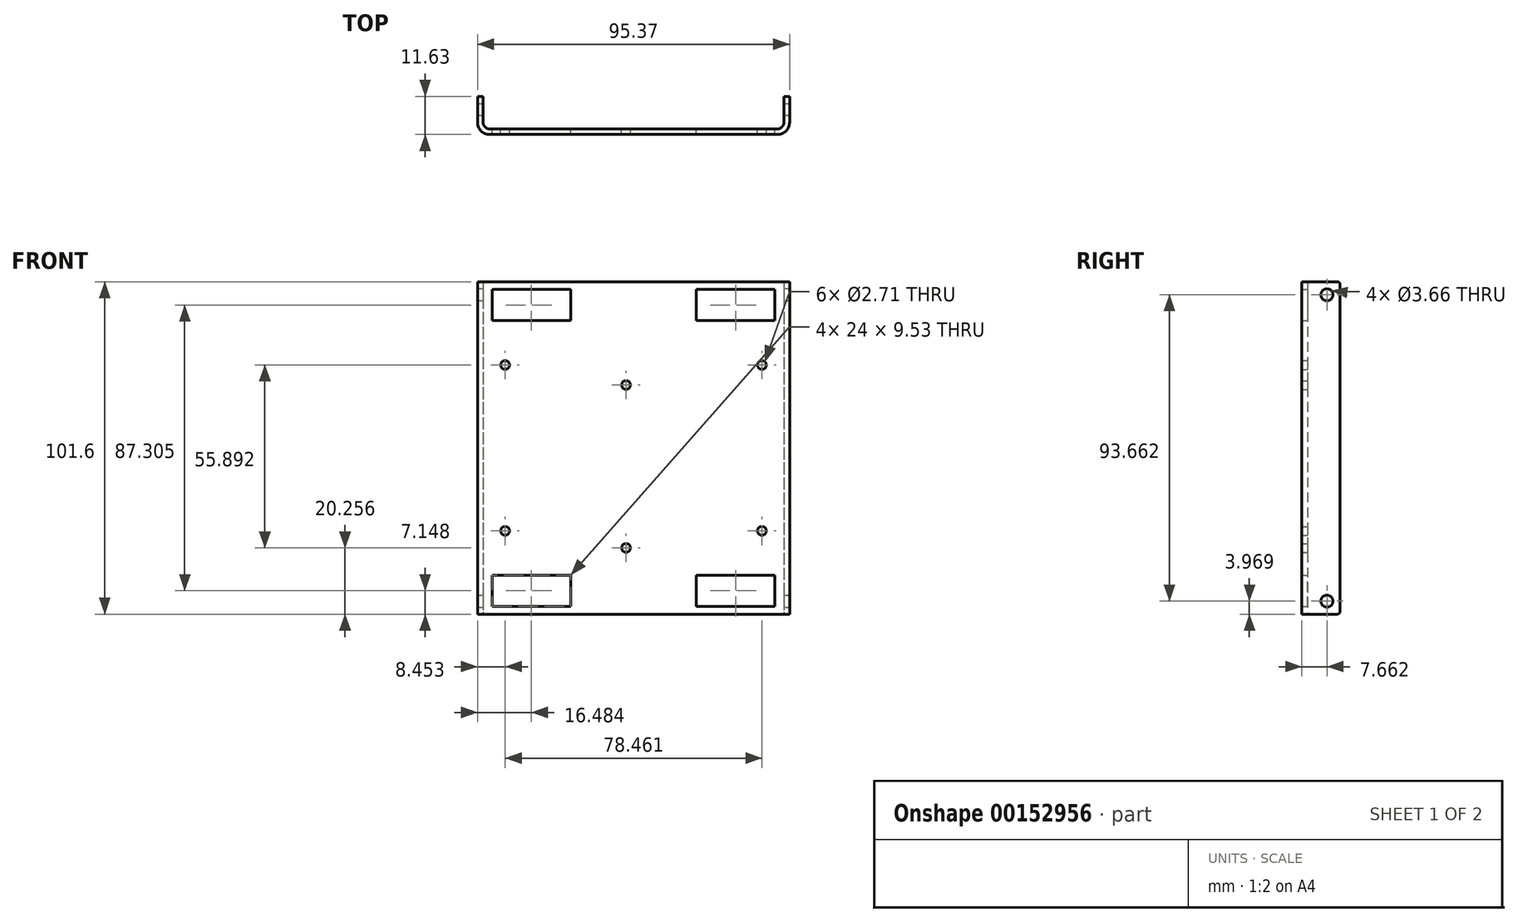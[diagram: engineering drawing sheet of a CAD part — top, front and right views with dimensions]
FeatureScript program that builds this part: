
annotation { "Feature Type Name" : "Feature", "Feature Type Description" : "" }
export const myFeature = defineFeature(function(context is Context, id is Id, definition is map)
    precondition{}
    {
        {
            var Q0;
            Q0=qCreatedBy(makeId("Top.planeOp"),FACE);
            var sketch = newSketch(context, id + "F0", { "sketchPlane" : qUnion([Q0])});
            skLineSegment(sketch, "E0.bottom", {"start": v(0, 0) * mm, "end": v(-91.95, 0) * mm});
            skLineSegment(sketch, "E0.top", {"start": v(1.7, -1.7) * mm, "end": v(-93.66, -1.7) * mm});
            skLineSegment(sketch, "E1.top", {"start": v(-91.95, 9.92) * mm, "end": v(-93.66, 9.92) * mm});
            skLineSegment(sketch, "E1.left", {"start": v(-91.95, 0) * mm, "end": v(-91.95, 9.92) * mm});
            skLineSegment(sketch, "E1.right", {"start": v(-93.66, -1.7) * mm, "end": v(-93.66, 9.92) * mm});
            skLineSegment(sketch, "E2.top", {"start": v(0, 9.92) * mm, "end": v(1.7, 9.92) * mm});
            skLineSegment(sketch, "E2.left", {"start": v(0, 0) * mm, "end": v(0, 9.92) * mm});
            skLineSegment(sketch, "E2.right", {"start": v(1.7, -1.7) * mm, "end": v(1.7, 9.92) * mm});
            skLineSegment(sketch, "E3", {"start": v(-45.98, 0) * mm, "end": v(-45.98, -1.7) * mm, "construction": true});
            skSolve(sketch);
        }
        {
            var Q0;
            Q0=qSketchRegion(id+"F0",true);
            extrude(context, id + "F1", {"entities" : qUnion([Q0]), "depth" : 101.6 * mm});
        }
        {
            var Q0;
            Q0=makeQuery(id+"F1.opExtrude","SWEPT_EDGE",EDGE,{"disambiguationData":[OSD([sQuery(id+"F0.wireOp",EDGE,"E0.top"),sQuery(id+"F0.wireOp",EDGE,"E2.right")])]});
            var Q1;
            Q1=makeQuery(id+"F1.opExtrude","SWEPT_EDGE",EDGE,{"disambiguationData":[OSD([sQuery(id+"F0.wireOp",EDGE,"E0.top"),sQuery(id+"F0.wireOp",EDGE,"E1.right")])]});
            var Q2;
            Q2=makeQuery(id+"FqNnmMD7oaRdpTN_1.opExtrude","CAP_EDGE",EDGE,{"disambiguationData":[OSD([sQuery(id+"FY5sMr6MULj5lJw_1.wireOp",EDGE,"W42EfhJi-fDm4-L9BW-folL-irsYfDskuzBk.top")])],"isStart":false});
            fillet(context, id + "F2", {"entities" : qUnion([Q0, Q1, Q2]), "radius" : 3.7 * mm, "tangentPropagation" : true, "allowEdgeOverflow" : false});
        }
        {
            var Q0;
            Q0=makeQuery(id+"F1.opExtrude","SWEPT_EDGE",EDGE,{"disambiguationData":[OSD([sQuery(id+"F0.wireOp",EDGE,"E0.bottom"),sQuery(id+"F0.wireOp",EDGE,"E2.left")])]});
            var Q1;
            Q1=makeQuery(id+"F1.opExtrude","SWEPT_EDGE",EDGE,{"disambiguationData":[OSD([sQuery(id+"F0.wireOp",EDGE,"E0.bottom"),sQuery(id+"F0.wireOp",EDGE,"E1.left")])]});
            fillet(context, id + "F3", {"entities" : qUnion([Q0, Q1]), "radius" : 1.98 * mm, "tangentPropagation" : true, "allowEdgeOverflow" : false});
        }
        {
            var Q0;
            Q0=makeQuery(id+"F1.opExtrude","SWEPT_FACE",FACE,{"disambiguationData":[OSD([sQuery(id+"F0.wireOp",EDGE,"E0.bottom")])]});
            var sketch = newSketch(context, id + "F4", { "sketchPlane" : qUnion([Q0])});
            skLineSegment(sketch, "E4", {"start": v(45.98, 101.6) * mm, "end": v(45.98, 0) * mm, "construction": true});
            skLineSegment(sketch, "E5.bottom", {"start": v(77.18, 94.45) * mm, "end": v(14.78, 94.45) * mm, "construction": true});
            skLineSegment(sketch, "E5.top", {"start": v(77.18, 7.15) * mm, "end": v(14.78, 7.15) * mm, "construction": true});
            skLineSegment(sketch, "E5.left", {"start": v(77.18, 94.45) * mm, "end": v(77.18, 7.15) * mm, "construction": true});
            skLineSegment(sketch, "E5.right", {"start": v(14.78, 94.45) * mm, "end": v(14.78, 7.15) * mm, "construction": true});
            skPoint(sketch, "E5.middle", {"position": v(45.98, 50.8) * mm});
            skLineSegment(sketch, "E6.bottom", {"start": v(89.18, 99.22) * mm, "end": v(65.18, 99.22) * mm});
            skLineSegment(sketch, "E6.top", {"start": v(89.18, 89.69) * mm, "end": v(65.18, 89.69) * mm});
            skLineSegment(sketch, "E6.left", {"start": v(89.18, 99.22) * mm, "end": v(89.18, 89.69) * mm});
            skLineSegment(sketch, "E6.right", {"start": v(65.18, 99.22) * mm, "end": v(65.18, 89.69) * mm});
            skPoint(sketch, "E6.middle", {"position": v(77.18, 94.45) * mm});
            skLineSegment(sketch, "E7.bottom", {"start": v(89.18, 2.38) * mm, "end": v(65.18, 2.38) * mm});
            skLineSegment(sketch, "E7.top", {"start": v(89.18, 11.91) * mm, "end": v(65.18, 11.91) * mm});
            skLineSegment(sketch, "E7.left", {"start": v(89.18, 2.38) * mm, "end": v(89.18, 11.91) * mm});
            skLineSegment(sketch, "E7.right", {"start": v(65.18, 2.38) * mm, "end": v(65.18, 11.91) * mm});
            skPoint(sketch, "E7.middle", {"position": v(77.18, 7.15) * mm});
            skLineSegment(sketch, "E8.bottom", {"start": v(2.78, 2.38) * mm, "end": v(26.78, 2.38) * mm});
            skLineSegment(sketch, "E8.top", {"start": v(2.78, 11.91) * mm, "end": v(26.78, 11.91) * mm});
            skLineSegment(sketch, "E8.left", {"start": v(2.78, 2.38) * mm, "end": v(2.78, 11.91) * mm});
            skLineSegment(sketch, "E8.right", {"start": v(26.78, 2.38) * mm, "end": v(26.78, 11.91) * mm});
            skPoint(sketch, "E8.middle", {"position": v(14.78, 7.15) * mm});
            skLineSegment(sketch, "E9.bottom", {"start": v(2.78, 99.22) * mm, "end": v(26.78, 99.22) * mm});
            skLineSegment(sketch, "E9.top", {"start": v(2.78, 89.69) * mm, "end": v(26.78, 89.69) * mm});
            skLineSegment(sketch, "E9.left", {"start": v(2.78, 99.22) * mm, "end": v(2.78, 89.69) * mm});
            skLineSegment(sketch, "E9.right", {"start": v(26.78, 99.22) * mm, "end": v(26.78, 89.69) * mm});
            skPoint(sketch, "E9.middle", {"position": v(14.78, 94.45) * mm});
            skLineSegment(sketch, "E10.bottom", {"start": v(89.18, 99.22) * mm, "end": v(89.97, 99.22) * mm, "construction": true});
            skLineSegment(sketch, "E10.top", {"start": v(89.18, 101.6) * mm, "end": v(89.97, 101.6) * mm, "construction": true});
            skLineSegment(sketch, "E10.left", {"start": v(89.18, 99.22) * mm, "end": v(89.18, 101.6) * mm, "construction": true});
            skLineSegment(sketch, "E10.right", {"start": v(89.97, 99.22) * mm, "end": v(89.97, 101.6) * mm, "construction": true});
            skLineSegment(sketch, "E11", {"start": v(89.18, 89.69) * mm, "end": v(89.18, 76.15) * mm, "construction": true});
            skLineSegment(sketch, "E12", {"start": v(89.18, 76.15) * mm, "end": v(85.2, 76.15) * mm, "construction": true});
            skLineSegment(sketch, "E13.bottom", {"start": v(85.2, 76.15) * mm, "end": v(6.75, 76.15) * mm, "construction": true});
            skLineSegment(sketch, "E13.top", {"start": v(85.2, 25.45) * mm, "end": v(6.75, 25.45) * mm, "construction": true});
            skLineSegment(sketch, "E13.left", {"start": v(85.2, 76.15) * mm, "end": v(85.2, 25.45) * mm, "construction": true});
            skLineSegment(sketch, "E13.right", {"start": v(6.75, 76.15) * mm, "end": v(6.75, 25.45) * mm, "construction": true});
            skCircle(sketch, "E14", {"center": v(85.2, 76.15) * mm, "radius": 1.35 * mm});
            skCircle(sketch, "E15", {"center": v(85.2, 25.45) * mm, "radius": 1.35 * mm});
            skCircle(sketch, "E16", {"center": v(6.75, 25.45) * mm, "radius": 1.35 * mm});
            skCircle(sketch, "E17", {"center": v(6.75, 76.15) * mm, "radius": 1.35 * mm});
            skSolve(sketch);
        }
        {
            var Q0;
            Q0 = qSketchRegion(id + "F4", true);
            var Q1;
            Q1=makeQuery(id+"F1.opExtrude","SWEPT_FACE",FACE,{"disambiguationData":[OSD([sQuery(id+"F0.wireOp",EDGE,"E0.top")])]});
            extrude(context, id + "F5", {"entities" : qUnion([Q0]), "operationType" : NewBodyOperationType.REMOVE, "endBound" : BoundingType.UP_TO_SURFACE, "oppositeDirection" : true, "endBoundEntityFace" : qUnion([Q1]), "depth" : 25.4 * mm});
        }
        {
            var Q0;
            Q0=makeQuery(id+"F1.opExtrude","SWEPT_FACE",FACE,{"disambiguationData":[OSD([sQuery(id+"F0.wireOp",EDGE,"E2.right")])]});
            var sketch = newSketch(context, id + "F6", { "sketchPlane" : qUnion([Q0])});
            skLineSegment(sketch, "E18.bottom", {"start": v(5.95, 101.6) * mm, "end": v(9.92, 101.6) * mm, "construction": true});
            skLineSegment(sketch, "E18.top", {"start": v(5.95, 97.63) * mm, "end": v(9.92, 97.63) * mm, "construction": true});
            skLineSegment(sketch, "E18.left", {"start": v(5.95, 101.6) * mm, "end": v(5.95, 97.63) * mm, "construction": true});
            skLineSegment(sketch, "E18.right", {"start": v(9.92, 101.6) * mm, "end": v(9.92, 97.63) * mm, "construction": true});
            skLineSegment(sketch, "E19.bottom", {"start": v(5.95, 0) * mm, "end": v(9.92, 0) * mm, "construction": true});
            skLineSegment(sketch, "E19.top", {"start": v(5.95, 3.97) * mm, "end": v(9.92, 3.97) * mm, "construction": true});
            skLineSegment(sketch, "E19.left", {"start": v(5.95, 0) * mm, "end": v(5.95, 3.97) * mm, "construction": true});
            skLineSegment(sketch, "E19.right", {"start": v(9.92, 0) * mm, "end": v(9.92, 3.97) * mm, "construction": true});
            skCircle(sketch, "E20", {"center": v(5.95, 97.63) * mm, "radius": 1.83 * mm});
            skCircle(sketch, "E21", {"center": v(5.95, 3.97) * mm, "radius": 1.83 * mm});
            skSolve(sketch);
        }
        {
            var Q0;
            Q0 = qSketchRegion(id + "F6", true);
            var Q1;
            Q1=makeQuery(id+"F1.opExtrude","SWEPT_FACE",FACE,{"disambiguationData":[OSD([sQuery(id+"F0.wireOp",EDGE,"E1.right")])]});
            extrude(context, id + "F7", {"entities" : qUnion([Q0]), "operationType" : NewBodyOperationType.REMOVE, "endBound" : BoundingType.UP_TO_SURFACE, "oppositeDirection" : true, "endBoundEntityFace" : qUnion([Q1]), "depth" : 25.4 * mm});
        }
        {
            var Q0;
            Q0=makeQuery(id+"F1.opExtrude","CAP_EDGE",EDGE,{"disambiguationData":[OSD([sQuery(id+"F0.wireOp",EDGE,"E1.top")])],"isStart":false});
            var Q1;
            Q1=makeQuery(id+"F1.opExtrude","CAP_EDGE",EDGE,{"disambiguationData":[OSD([sQuery(id+"F0.wireOp",EDGE,"E1.top")])],"isStart":true});
            var Q2;
            Q2=makeQuery(id+"F1.opExtrude","CAP_EDGE",EDGE,{"disambiguationData":[OSD([sQuery(id+"F0.wireOp",EDGE,"E2.top")])],"isStart":true});
            var Q3;
            Q3=makeQuery(id+"F1.opExtrude","CAP_EDGE",EDGE,{"disambiguationData":[OSD([sQuery(id+"F0.wireOp",EDGE,"E2.top")])],"isStart":false});
            fillet(context, id + "F8", {"entities" : qUnion([Q0, Q1, Q2, Q3]), "radius" : 0.76 * mm, "tangentPropagation" : true, "allowEdgeOverflow" : false});
        }
        {
            var Q0;
            Q0=makeQuery(id+"F1.opExtrude","SWEPT_FACE",FACE,{"disambiguationData":[OSD([sQuery(id+"F0.wireOp",EDGE,"E0.bottom")])]});
            var sketch = newSketch(context, id + "F9", { "sketchPlane" : qUnion([Q0])});
            skLineSegment(sketch, "E22", {"start": v(54.22, 50.8) * mm, "end": v(66.87, 50.8) * mm, "construction": true});
            skLineSegment(sketch, "E23", {"start": v(54.22, 50.8) * mm, "end": v(25.09, 50.8) * mm, "construction": true});
            skLineSegment(sketch, "E24", {"start": v(25.09, 50.8) * mm, "end": v(1.98, 50.8) * mm, "construction": true});
            skLineSegment(sketch, "E25", {"start": v(66.87, 50.8) * mm, "end": v(89.97, 50.8) * mm, "construction": true});
            skLineSegment(sketch, "E26", {"start": v(54.22, 50.8) * mm, "end": v(54.22, 45.15) * mm, "construction": true});
            skLineSegment(sketch, "E27", {"start": v(54.22, 45.15) * mm, "end": v(48.27, 45.15) * mm, "construction": true});
            skLineSegment(sketch, "E28", {"start": v(48.27, 20.26) * mm, "end": v(48.27, 70.04) * mm, "construction": true});
            skCircle(sketch, "E29", {"center": v(48.27, 20.26) * mm, "radius": 1.35 * mm});
            skCircle(sketch, "E30", {"center": v(48.27, 70.04) * mm, "radius": 1.35 * mm});
            skSolve(sketch);
        }
        {
            var Q0;
            Q0=makeQuery(id+"F9.imprint","IMPRINT",FACE,{"disambiguationData":[TD([[makeQuery(id+"F9.imprint","IMPRINT",EDGE,{"derivedFrom":sQuery(id+"F9.wireOp",EDGE,"E30")}),1.0]])]});
            var Q1;
            Q1=makeQuery(id+"F9.imprint","IMPRINT",FACE,{"disambiguationData":[TD([[makeQuery(id+"F9.imprint","IMPRINT",EDGE,{"derivedFrom":sQuery(id+"F9.wireOp",EDGE,"E29")}),1.0]])]});
            var Q2;
            Q2=makeQuery(id+"F1.opExtrude","SWEPT_FACE",FACE,{"disambiguationData":[OSD([sQuery(id+"F0.wireOp",EDGE,"E0.top")])]});
            extrude(context, id + "F10", {"entities" : qUnion([Q0, Q1]), "operationType" : NewBodyOperationType.REMOVE, "endBound" : BoundingType.UP_TO_SURFACE, "oppositeDirection" : true, "endBoundEntityFace" : qUnion([Q2]), "depth" : 25.4 * mm});
        }
    });
